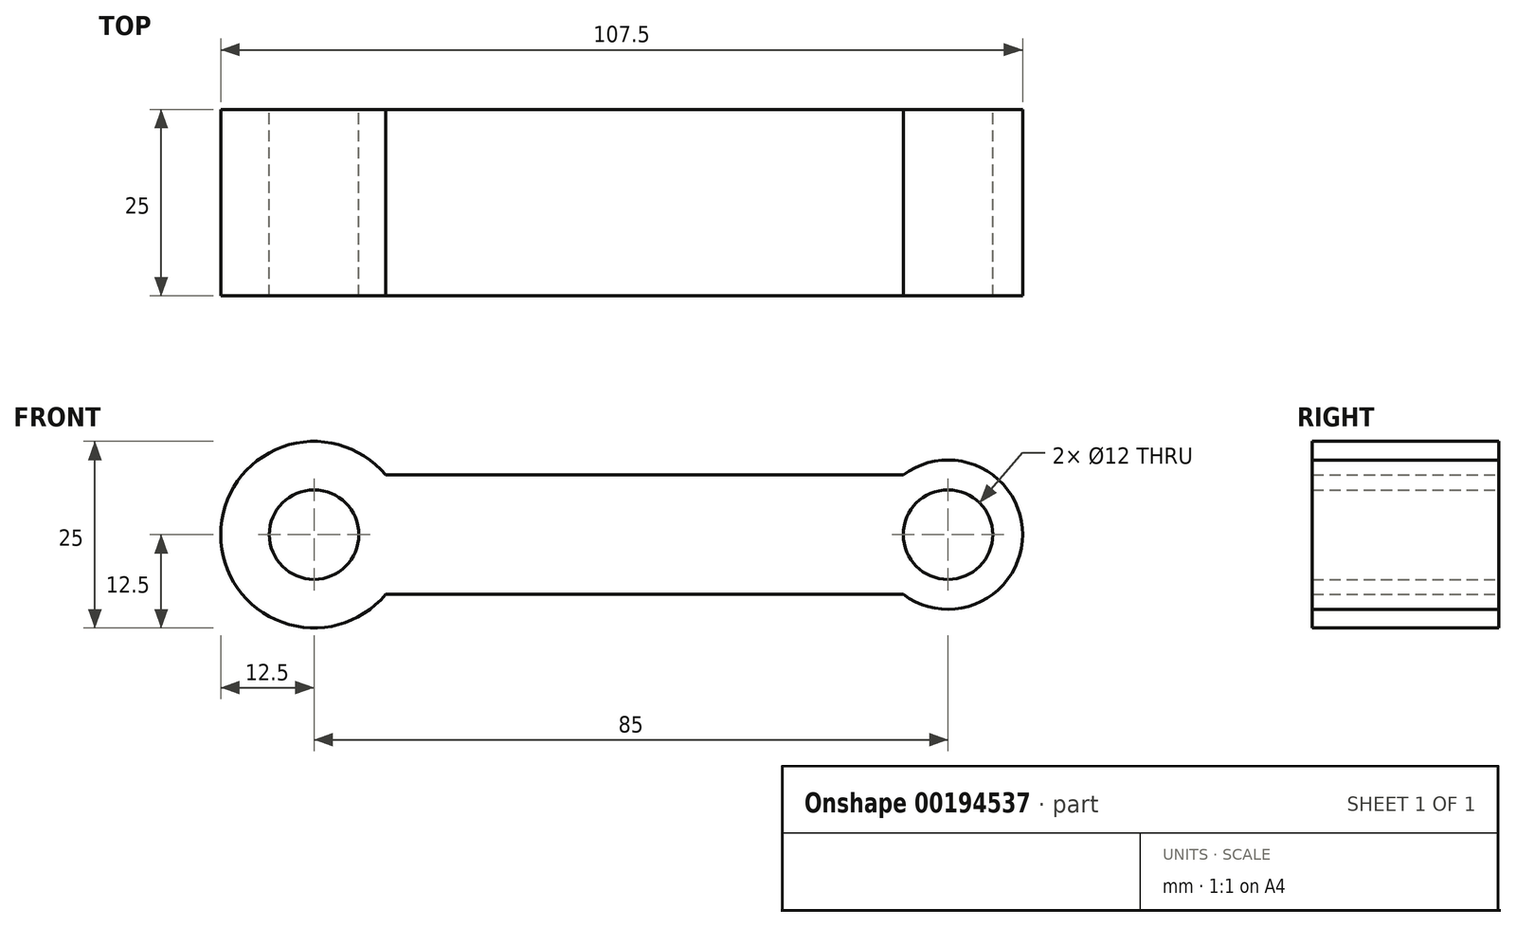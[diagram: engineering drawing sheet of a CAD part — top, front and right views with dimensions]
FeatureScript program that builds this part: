
annotation { "Feature Type Name" : "Feature", "Feature Type Description" : "" }
export const myFeature = defineFeature(function(context is Context, id is Id, definition is map)
    precondition{}
    {
        {
            var Q0;
            Q0=qCreatedBy(makeId("Front.planeOp"),FACE);
            var sketch = newSketch(context, id + "F0", { "sketchPlane" : qUnion([Q0])});
            skCircle(sketch, "E0", {"center": v(0, 0) * mm, "radius": 12.5 * mm});
            skCircle(sketch, "E1", {"center": v(85, 0) * mm, "radius": 10 * mm});
            skLineSegment(sketch, "E2", {"start": v(85, 0) * mm, "end": v(0, 0) * mm, "construction": true});
            skLineSegment(sketch, "E3", {"start": v(9.6, 8) * mm, "end": v(79, 8) * mm});
            skLineSegment(sketch, "E4.MirrorCS", {"start": v(9.6, -8) * mm, "end": v(79, -8) * mm});
            skCircle(sketch, "E5", {"center": v(0, 0) * mm, "radius": 6 * mm});
            skCircle(sketch, "E6", {"center": v(85, 0) * mm, "radius": 6 * mm});
            skSolve(sketch);
        }
        {
            var Q0;
            Q0 = qSketchRegion(id + "F0", true);
            extrude(context, id + "F1", {"entities" : qUnion([Q0]), "depth" : 25 * mm});
        }
    });
